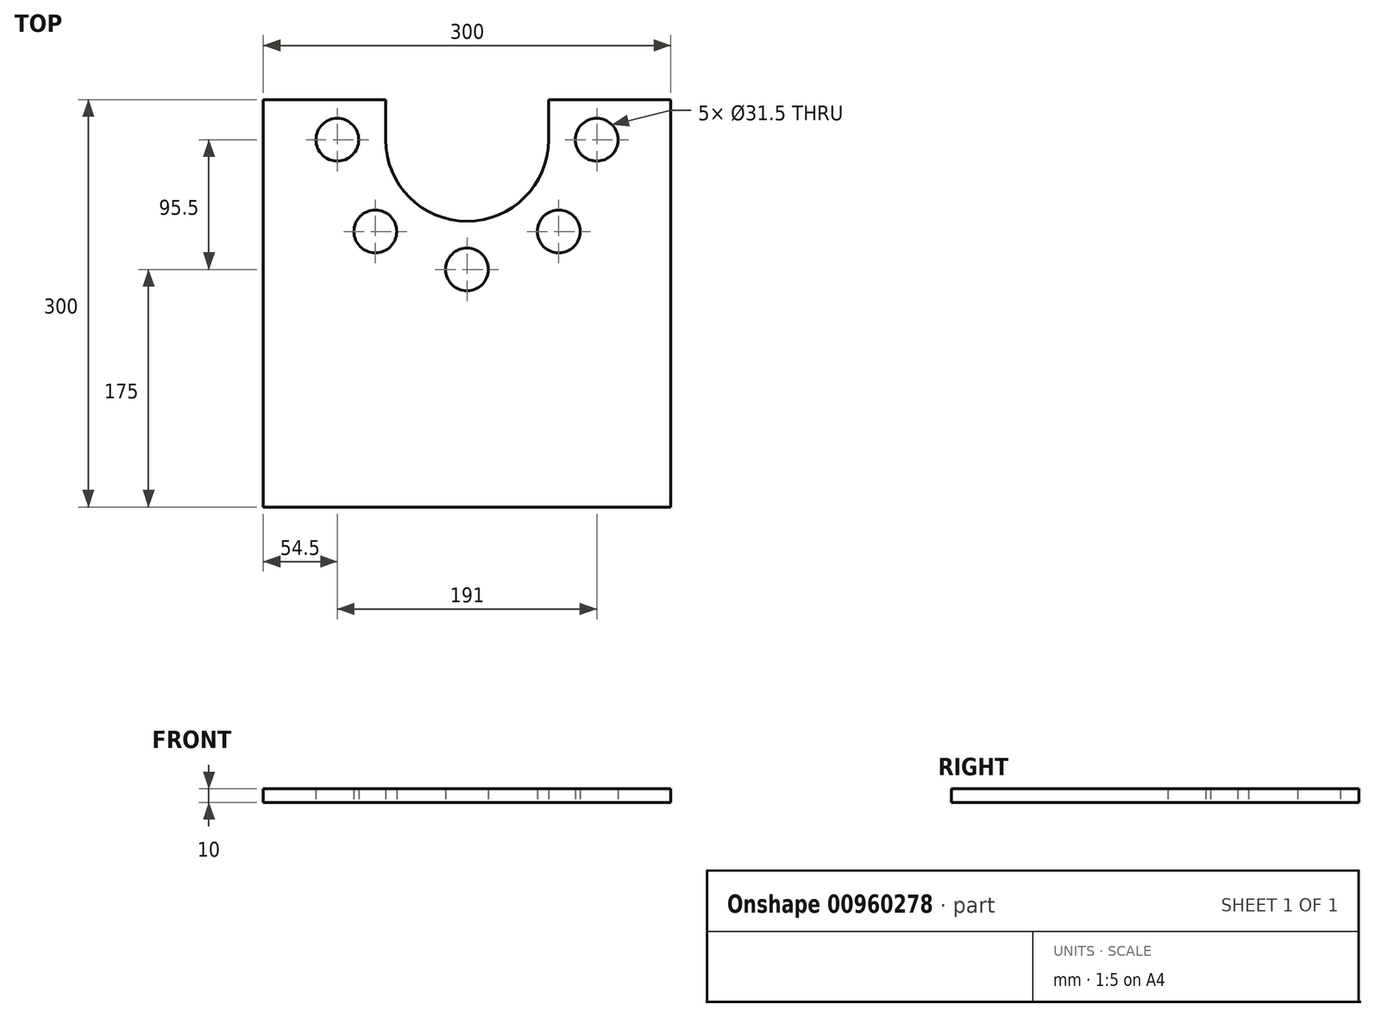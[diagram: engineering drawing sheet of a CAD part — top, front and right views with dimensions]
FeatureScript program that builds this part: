
annotation { "Feature Type Name" : "Feature", "Feature Type Description" : "" }
export const myFeature = defineFeature(function(context is Context, id is Id, definition is map)
    precondition{}
    {
        {
            var Q0;
            Q0=qCreatedBy(makeId("Top.planeOp"),FACE);
            var sketch = newSketch(context, id + "F0", { "sketchPlane" : qUnion([Q0])});
            skCircle(sketch, "E0", {"center": v(0, 0) * mm, "radius": 95.5 * mm});
            skLineSegment(sketch, "E1", {"start": v(0, 0) * mm, "end": v(0, -95.5) * mm});
            skCircle(sketch, "E2.cCircle", {"center": v(182.74, 56.92) * mm, "radius": 13.5 * mm, "construction": true});
            skLineSegment(sketch, "E2.0", {"start": v(190.47, 43.39) * mm, "end": v(174.88, 43.46) * mm});
            skLineSegment(sketch, "E2.1", {"start": v(174.88, 43.46) * mm, "end": v(167.15, 57) * mm});
            skLineSegment(sketch, "E2.2", {"start": v(167.15, 57) * mm, "end": v(175, 70.46) * mm});
            skLineSegment(sketch, "E2.3", {"start": v(175, 70.46) * mm, "end": v(190.6, 70.39) * mm});
            skLineSegment(sketch, "E2.4", {"start": v(190.6, 70.39) * mm, "end": v(198.33, 56.85) * mm});
            skLineSegment(sketch, "E2.5", {"start": v(198.33, 56.85) * mm, "end": v(190.47, 43.39) * mm});
            skPoint(sketch, "E2.0.midPoint", {"position": v(182.68, 43.42) * mm});
            skCircle(sketch, "E3", {"center": v(0, -95.5) * mm, "radius": 15.75 * mm});
            skCircle(sketch, "E4.1.0", {"center": v(67.53, -67.53) * mm, "radius": 15.75 * mm});
            skCircle(sketch, "E4.2.0", {"center": v(95.5, 0) * mm, "radius": 15.75 * mm});
            skCircle(sketch, "E4.3.0", {"center": v(67.53, 67.53) * mm, "radius": 15.75 * mm});
            skCircle(sketch, "E4.4.0", {"center": v(0, 95.5) * mm, "radius": 15.75 * mm});
            skCircle(sketch, "E4.5.0", {"center": v(-67.53, 67.53) * mm, "radius": 15.75 * mm});
            skCircle(sketch, "E4.6.0", {"center": v(-95.5, 0) * mm, "radius": 15.75 * mm});
            skCircle(sketch, "E4.7.0", {"center": v(-67.53, -67.53) * mm, "radius": 15.75 * mm});
            skCircle(sketch, "E5", {"center": v(0, 0) * mm, "radius": 60 * mm});
            skLineSegment(sketch, "E6", {"start": v(150, -95.5) * mm, "end": v(150, 29.5) * mm});
            skLineSegment(sketch, "E7", {"start": v(150, 29.5) * mm, "end": v(-150, 29.5) * mm});
            skLineSegment(sketch, "E8", {"start": v(-150, 29.5) * mm, "end": v(-150, -270.5) * mm});
            skLineSegment(sketch, "E9", {"start": v(-150, -270.5) * mm, "end": v(150, -270.5) * mm});
            skLineSegment(sketch, "E10", {"start": v(150, -270.5) * mm, "end": v(150, -95.5) * mm});
            skCircle(sketch, "E11", {"center": v(0, 0) * mm, "radius": 115 * mm});
            skLineSegment(sketch, "E12", {"start": v(-60, 0) * mm, "end": v(-60, 29.5) * mm});
            skLineSegment(sketch, "E13", {"start": v(60, 0) * mm, "end": v(60, 29.5) * mm});
            skSolve(sketch);
        }
        {
            var Q0;
            {var subQ4=sQuery(id+"F0.wireOp",EDGE,"E6");Q0=makeQuery(id+"F0.imprint","IMPRINT",FACE,{"disambiguationData":[TD([[makeQuery(id+"F0.imprint","IMPRINT",EDGE,{"derivedFrom":subQ4}),1.0]])]});}
            var Q1;
            {var subQ1=sQuery(id+"F0.wireOp",EDGE,"E0");var subQ4=sQuery(id+"F0.wireOp",EDGE,"E7");var subQ17=makeQuery(id+"F0.imprint","INTERSECT",VERTEX,{"disambiguationData":[OD(0.0)],"derivedFrom":[subQ1,subQ4]});Q1=makeQuery(id+"F0.imprint","IMPRINT",FACE,{"disambiguationData":[TD([[makeQuery(id+"F0.imprint","IMPRINT",EDGE,{"disambiguationData":[TD([[subQ17,1.0]])],"derivedFrom":subQ1}),-1.0]])]});}
            var Q2;
            {var subQ5=sQuery(id+"F0.wireOp",EDGE,"E7");var subQ6=sQuery(id+"F0.wireOp",EDGE,"E0");var subQ7=makeQuery(id+"F0.imprint","INTERSECT",VERTEX,{"disambiguationData":[OD(1.0)],"derivedFrom":[subQ6,subQ5]});Q2=makeQuery(id+"F0.imprint","IMPRINT",FACE,{"disambiguationData":[TD([[makeQuery(id+"F0.imprint","IMPRINT",EDGE,{"disambiguationData":[TD([[subQ7,-1.0]])],"derivedFrom":subQ6}),1.0]])]});}
            var Q3;
            {var subQ6=sQuery(id+"F0.wireOp",EDGE,"E0");var subQ11=sQuery(id+"F0.wireOp",EDGE,"E7");var subQ12=makeQuery(id+"F0.imprint","INTERSECT",VERTEX,{"disambiguationData":[OD(0.0)],"derivedFrom":[subQ6,subQ11]});Q3=makeQuery(id+"F0.imprint","IMPRINT",FACE,{"disambiguationData":[TD([[makeQuery(id+"F0.imprint","IMPRINT",EDGE,{"disambiguationData":[TD([[subQ12,1.0]])],"derivedFrom":subQ6}),1.0]])]});}
            extrude(context, id + "F1", {"entities" : qUnion([Q0, Q1, Q2, Q3]), "depth" : 10 * mm, "offsetDistance" : 25 * mm});
        }
    });
